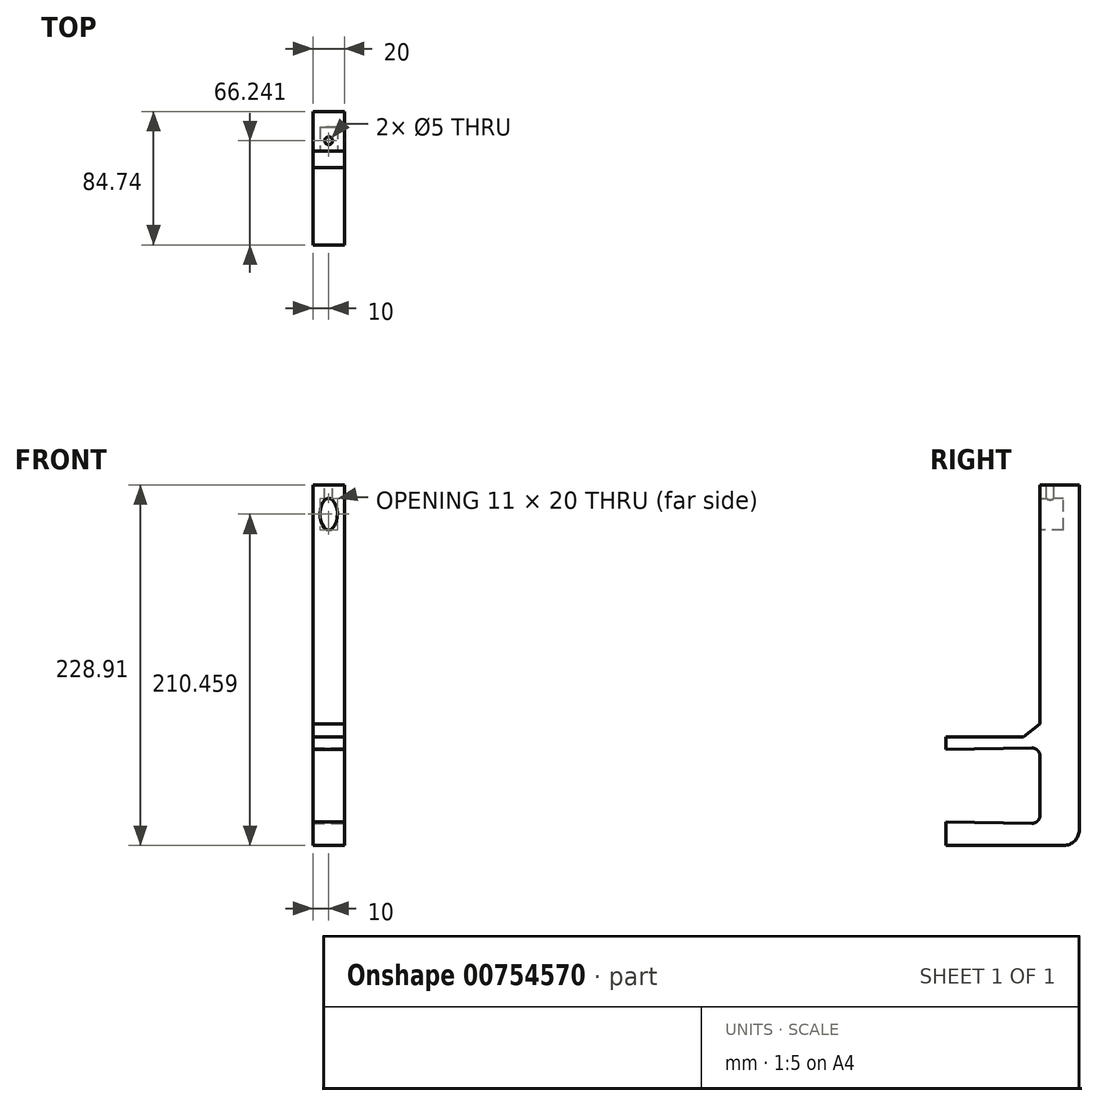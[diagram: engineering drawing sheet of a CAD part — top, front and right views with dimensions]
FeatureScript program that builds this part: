
annotation { "Feature Type Name" : "Feature", "Feature Type Description" : "" }
export const myFeature = defineFeature(function(context is Context, id is Id, definition is map)
    precondition{}
    {
        {
            var Q0;
            Q0=qCreatedBy(makeId("Right.planeOp"),FACE);
            var sketch = newSketch(context, id + "F0", { "sketchPlane" : qUnion([Q0])});
            skLineSegment(sketch, "E0", {"start": v(-38.47, 17.76) * mm, "end": v(21.27, 18.8) * mm});
            skLineSegment(sketch, "E1", {"start": v(21.27, 18.8) * mm, "end": v(21.27, -29.2) * mm});
            skLineSegment(sketch, "E2", {"start": v(21.27, -29.2) * mm, "end": v(-38.47, -28.15) * mm});
            skLineSegment(sketch, "E3", {"start": v(-38.47, -28.15) * mm, "end": v(-38.47, -43.15) * mm});
            skLineSegment(sketch, "E4", {"start": v(-38.47, -43.15) * mm, "end": v(36.27, -43.15) * mm});
            skLineSegment(sketch, "E5", {"start": v(46.27, -33.15) * mm, "end": v(46.27, 185.76) * mm});
            skLineSegment(sketch, "E6", {"start": v(46.27, 185.76) * mm, "end": v(21.27, 185.76) * mm});
            skLineSegment(sketch, "E7", {"start": v(-38.47, 25.76) * mm, "end": v(-38.47, 17.76) * mm});
            skLineSegment(sketch, "E8", {"start": v(10.8, 25.76) * mm, "end": v(-38.47, 25.76) * mm});
            skLineSegment(sketch, "E9", {"start": v(10.8, 25.76) * mm, "end": v(21.27, 34.02) * mm});
            skLineSegment(sketch, "E10", {"start": v(21.27, 34.02) * mm, "end": v(21.27, 34.02) * mm});
            skLineSegment(sketch, "E11", {"start": v(21.27, 185.76) * mm, "end": v(21.27, 34.02) * mm});
            skPoint(sketch, "E12.visualSharp", {"position": v(46.27, -43.15) * mm});
            skArc(sketch, "E12.filletArc", {"start": v(36.27, -43.15) * mm, "mid": v(43.34, -40.23) * mm, "end": v(46.27, -33.15) * mm});
            skSolve(sketch);
        }
        {
            var Q0;
            Q0=makeQuery(id+"F0.imprint","IMPRINT",FACE,{"disambiguationData":[TD([[makeQuery(id+"F0.imprint","IMPRINT",EDGE,{"derivedFrom":sQuery(id+"F0.wireOp",EDGE,"E0")}),1.0]])]});
            extrude(context, id + "F1", {"entities" : qUnion([Q0]), "depth" : 20 * mm, "offsetDistance" : 25 * mm});
        }
        {
            var Q0;
            Q0=makeQuery(id+"F1.opExtrude","SWEPT_EDGE",EDGE,{"disambiguationData":[OSD([sQuery(id+"F0.wireOp",EDGE,"E0"),sQuery(id+"F0.wireOp",EDGE,"E1")])]});
            var Q1;
            Q1=makeQuery(id+"F1.opExtrude","SWEPT_EDGE",EDGE,{"disambiguationData":[OSD([sQuery(id+"F0.wireOp",EDGE,"E1"),sQuery(id+"F0.wireOp",EDGE,"E2")])]});
            fillet(context, id + "F2", {"entities" : qUnion([Q0, Q1]), "radius" : 5 * mm, "tangentPropagation" : true, "allowEdgeOverflow" : false});
        }
        {
            var Q0;
            Q0=makeQuery(id+"F1.opExtrude","SWEPT_FACE",FACE,{"disambiguationData":[OSD([sQuery(id+"F0.wireOp",EDGE,"E11")])]});
            var sketch = newSketch(context, id + "F3", { "sketchPlane" : qUnion([Q0])});
            skEllipse(sketch, "E13", {"center": v(10, 167.3) * mm, "majorRadius": 10 * mm, "minorRadius": 5.5 * mm, "majorAxis": v(0, -1)});
            skPoint(sketch, "E13.centerSnap0", {"position": v(10, 185.76) * mm});
            skSolve(sketch);
        }
        {
            var Q0;
            Q0=makeQuery(id+"F3.imprint","IMPRINT",FACE,{"disambiguationData":[TD([[makeQuery(id+"F3.imprint","IMPRINT",EDGE,{"derivedFrom":sQuery(id+"F3.wireOp",EDGE,"E13")}),1.0]])]});
            extrude(context, id + "F4", {"entities" : qUnion([Q0]), "operationType" : NewBodyOperationType.REMOVE, "oppositeDirection" : true, "depth" : 15 * mm, "offsetDistance" : 25 * mm});
        }
        {
            var Q0;
            Q0=makeQuery(id+"F1.opExtrude","SWEPT_FACE",FACE,{"disambiguationData":[OSD([sQuery(id+"F0.wireOp",EDGE,"E6")])]});
            var sketch = newSketch(context, id + "F5", { "sketchPlane" : qUnion([Q0])});
            skPoint(sketch, "E14", {"position": v(10, 27.77) * mm});
            skPoint(sketch, "E14.positionSnap0", {"position": v(10, 21.27) * mm});
            skSolve(sketch);
        }
        {
            var Q0;
            Q0=sQuery(id+"F5.wireOp",VERTEX,"E14");
            var Q1;
            Q1=makeQuery(id+"F1.opExtrude","SWEPT_BODY",BODY,{"disambiguationData":[OSD([sQuery(id+"F0.wireOp",EDGE,"E0"),sQuery(id+"F0.wireOp",EDGE,"E1"),sQuery(id+"F0.wireOp",EDGE,"E2"),sQuery(id+"F0.wireOp",EDGE,"E3"),sQuery(id+"F0.wireOp",EDGE,"E4"),sQuery(id+"F0.wireOp",EDGE,"E5"),sQuery(id+"F0.wireOp",EDGE,"E6"),sQuery(id+"F0.wireOp",EDGE,"E7"),sQuery(id+"F0.wireOp",EDGE,"E8"),sQuery(id+"F0.wireOp",EDGE,"E9"),sQuery(id+"F0.wireOp",EDGE,"E11"),sQuery(id+"F0.wireOp",EDGE,"E12.filletArc")])]});
            hole(context, id + "F6", {"style" : HoleStyle.SIMPLE, "endStyle" : HoleEndStyle.BLIND, "holeDiameter" : 5 * mm, "majorDiameter" : 5 * mm, "holeDepth" : 12 * mm, "isTappedThrough" : true, "tappedDepth" : 12 * mm, "tapClearance" : 3, "locations" : qUnion([Q0]), "scope" : qUnion([Q1])});
        }
    });
